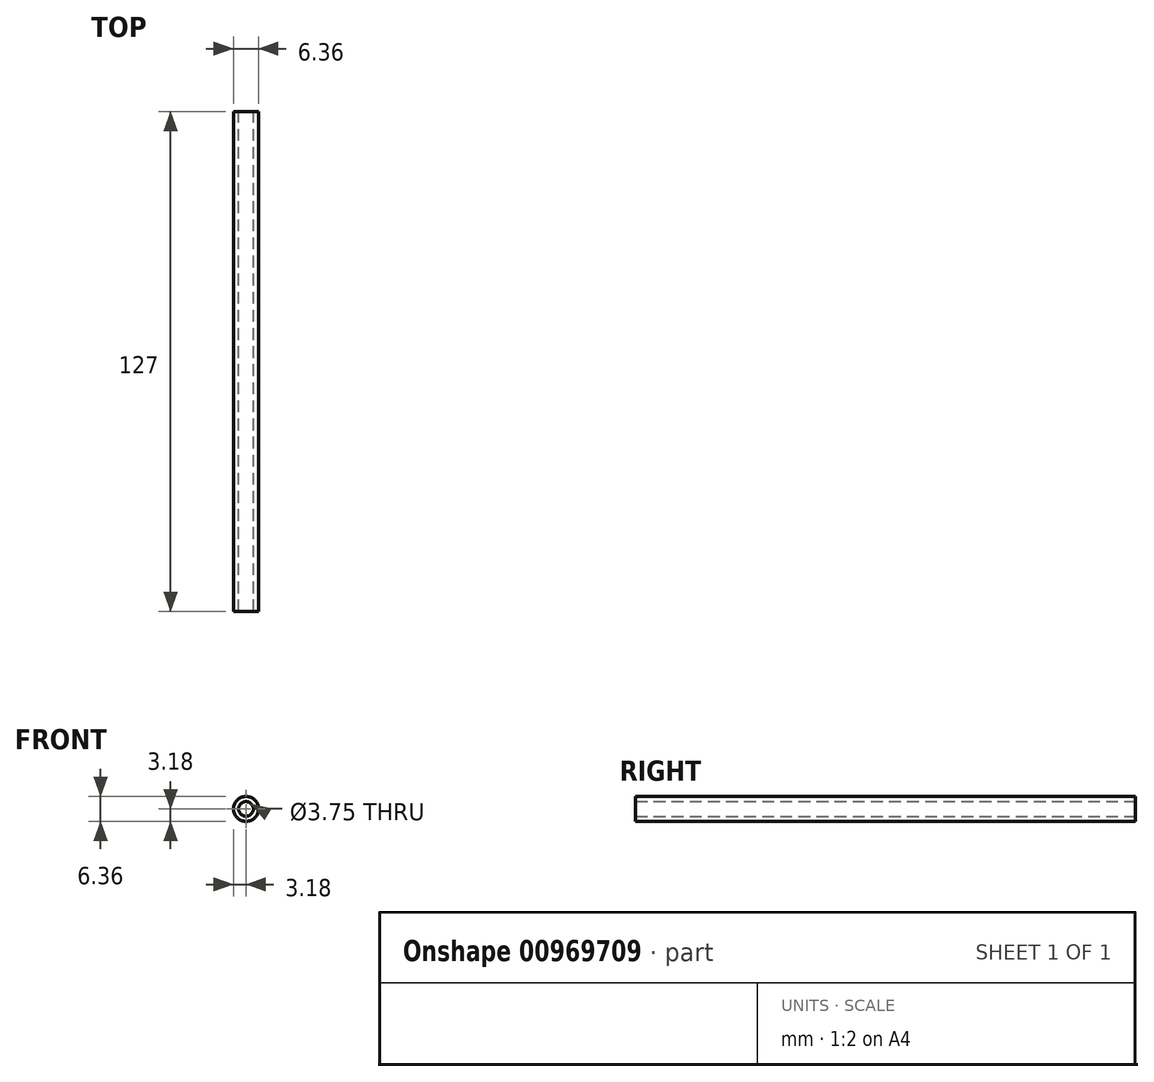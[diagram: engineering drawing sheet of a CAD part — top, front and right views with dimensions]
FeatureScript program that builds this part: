
annotation { "Feature Type Name" : "Feature", "Feature Type Description" : "" }
export const myFeature = defineFeature(function(context is Context, id is Id, definition is map)
    precondition{}
    {
        {
            var Q0;
            Q0=qCreatedBy(makeId("Front.planeOp"),FACE);
            var sketch = newSketch(context, id + "F0", { "sketchPlane" : qUnion([Q0])});
            skCircle(sketch, "E0", {"center": v(0, 0) * mm, "radius": 3.18 * mm});
            skCircle(sketch, "E1", {"center": v(0, 0) * mm, "radius": 1.88 * mm});
            skSolve(sketch);
        }
        {
            var Q0;
            Q0=makeQuery(id+"F0.imprint","IMPRINT",FACE,{"disambiguationData":[TD([[makeQuery(id+"F0.imprint","IMPRINT",EDGE,{"derivedFrom":sQuery(id+"F0.wireOp",EDGE,"E0")}),1.0]])]});
            extrude(context, id + "F1", {"entities" : qUnion([Q0]), "depth" : 127 * mm, "offsetDistance" : 25.4 * mm});
        }
    });
